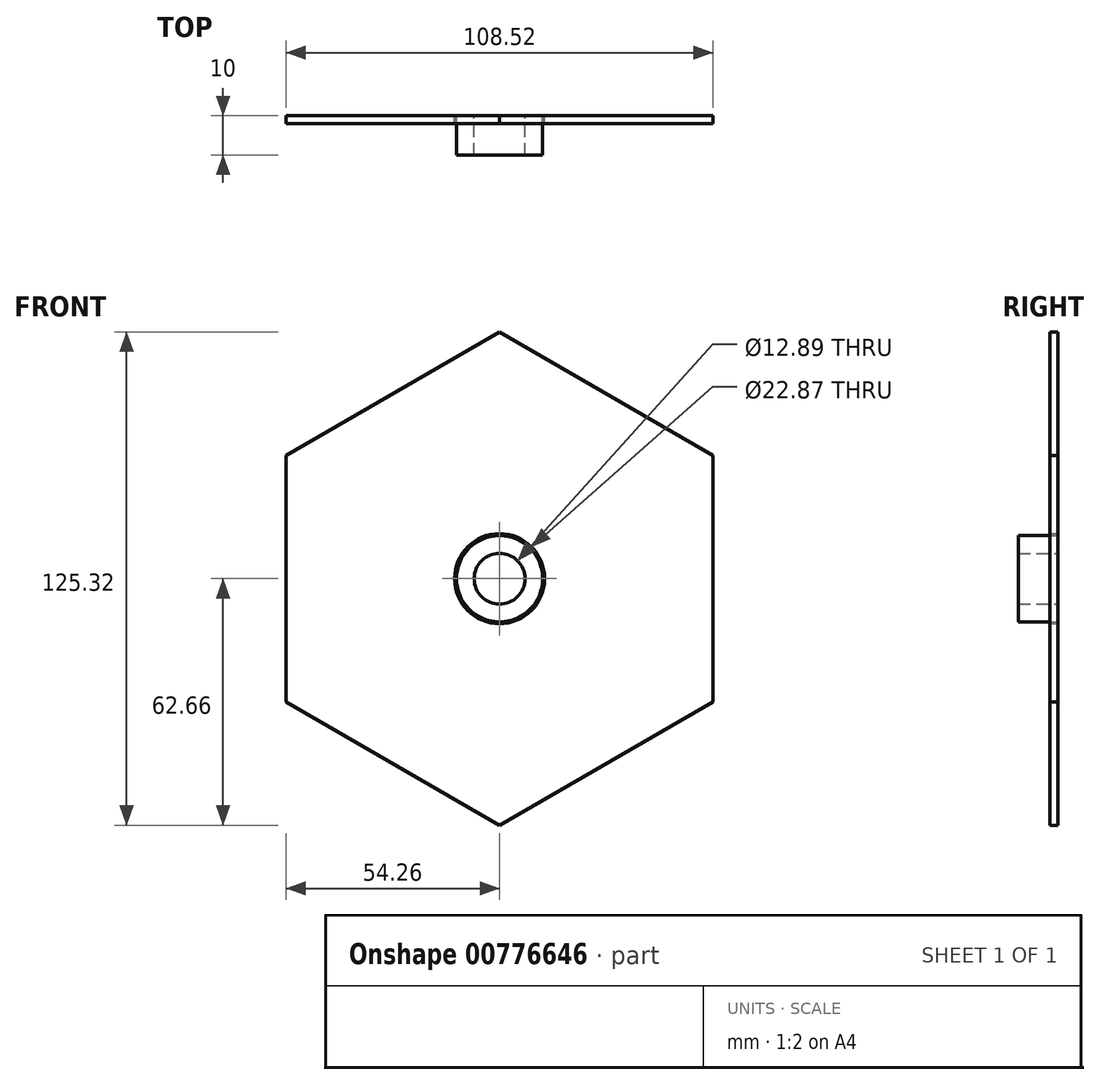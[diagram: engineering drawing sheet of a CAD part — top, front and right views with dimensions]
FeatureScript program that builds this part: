
annotation { "Feature Type Name" : "Feature", "Feature Type Description" : "" }
export const myFeature = defineFeature(function(context is Context, id is Id, definition is map)
    precondition{}
    {
        {
            var Q0;
            Q0=qCreatedBy(makeId("Front.planeOp"),FACE);
            var sketch = newSketch(context, id + "F0", { "sketchPlane" : qUnion([Q0])});
            skCircle(sketch, "E0.cCircle", {"center": v(0, 0) * mm, "radius": 62.66 * mm, "construction": true});
            skLineSegment(sketch, "E0.0", {"start": v(0, -62.66) * mm, "end": v(-54.26, -31.33) * mm});
            skLineSegment(sketch, "E0.1", {"start": v(-54.26, -31.33) * mm, "end": v(-54.26, 31.33) * mm});
            skLineSegment(sketch, "E0.2", {"start": v(-54.26, 31.33) * mm, "end": v(0, 62.66) * mm});
            skLineSegment(sketch, "E0.3", {"start": v(0, 62.66) * mm, "end": v(54.26, 31.33) * mm});
            skLineSegment(sketch, "E0.4", {"start": v(54.26, 31.33) * mm, "end": v(54.26, -31.33) * mm});
            skLineSegment(sketch, "E0.5", {"start": v(54.26, -31.33) * mm, "end": v(0, -62.66) * mm});
            skCircle(sketch, "E1", {"center": v(0, 0) * mm, "radius": 11.43 * mm});
            skCircle(sketch, "E2", {"center": v(0, 0) * mm, "radius": 6.27 * mm});
            skSolve(sketch);
        }
        {
            var Q0;
            Q0=makeQuery(id+"F0.imprint","IMPRINT",FACE,{"disambiguationData":[TD([[makeQuery(id+"F0.imprint","IMPRINT",EDGE,{"derivedFrom":sQuery(id+"F0.wireOp",EDGE,"E0.0")}),-1.0]])]});
            extrude(context, id + "F1", {"entities" : qUnion([Q0]), "depth" : 2 * mm, "offsetDistance" : 25 * mm});
        }
        {
            var Q0;
            Q0=qCreatedBy(makeId("Front.planeOp"),FACE);
            var sketch = newSketch(context, id + "F2", { "sketchPlane" : qUnion([Q0])});
            skCircle(sketch, "E3", {"center": v(0, 0) * mm, "radius": 10.95 * mm});
            skCircle(sketch, "E4", {"center": v(0, 0) * mm, "radius": 6.45 * mm});
            skSolve(sketch);
        }
        {
            var Q0;
            Q0 = qSketchRegion(id + "F2", true);
            extrude(context, id + "F3", {"entities" : qUnion([Q0]), "depth" : 10 * mm, "offsetDistance" : 25 * mm});
        }
    });
